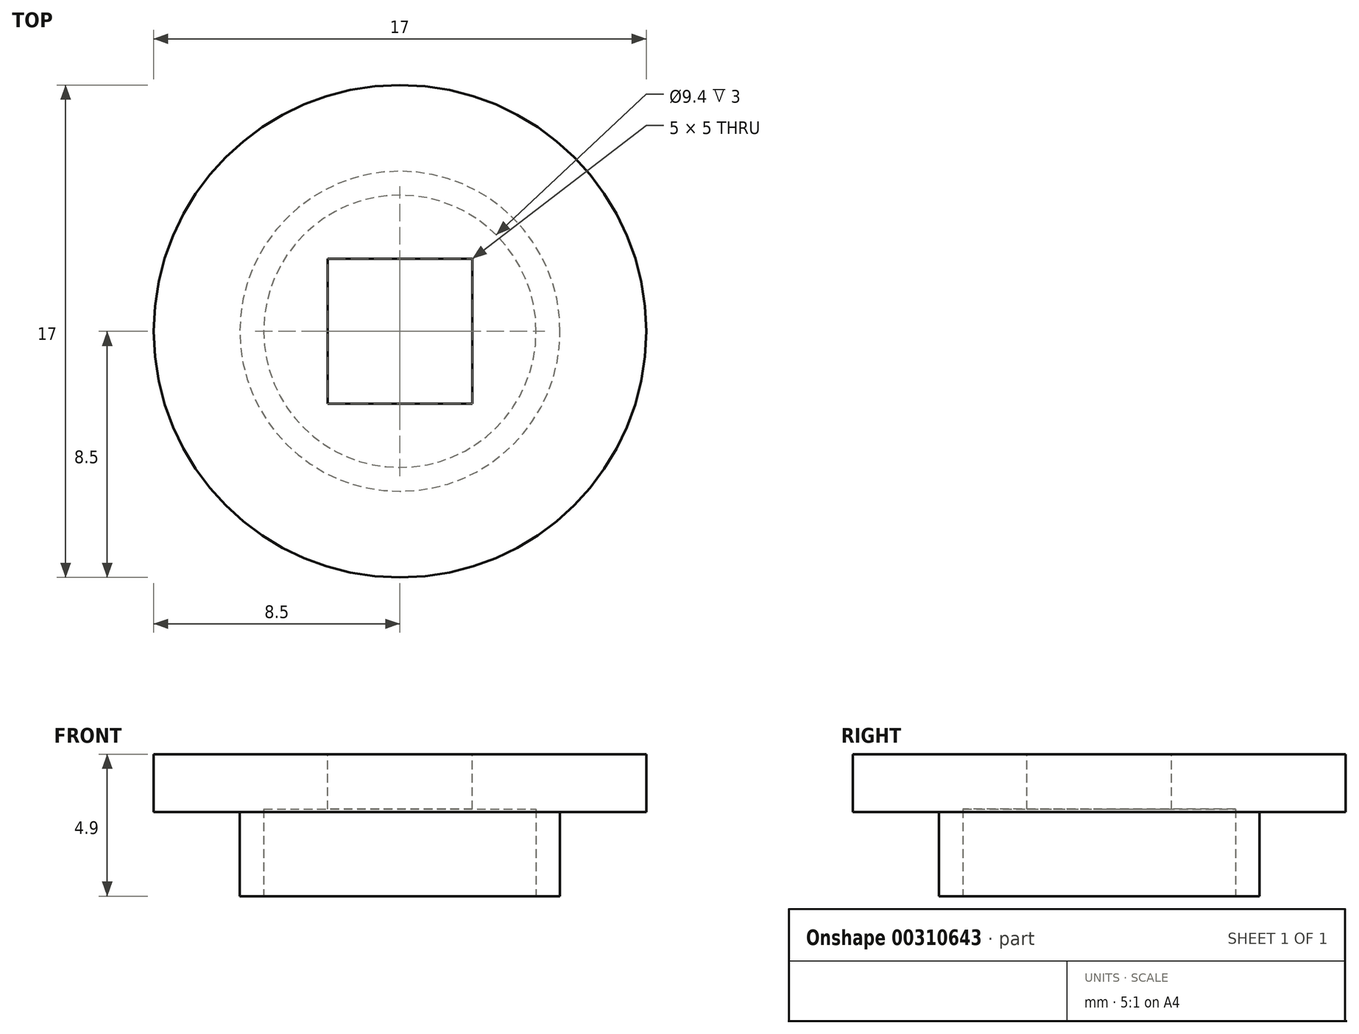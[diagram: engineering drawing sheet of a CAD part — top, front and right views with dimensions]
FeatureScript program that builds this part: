
annotation { "Feature Type Name" : "Feature", "Feature Type Description" : "" }
export const myFeature = defineFeature(function(context is Context, id is Id, definition is map)
    precondition{}
    {
        {
            var Q0;
            Q0=qCreatedBy(makeId("Top.planeOp"),FACE);
            var sketch = newSketch(context, id + "F0", { "sketchPlane" : qUnion([Q0])});
            skCircle(sketch, "E0", {"center": v(0, 0) * mm, "radius": 8.5 * mm});
            skSolve(sketch);
        }
        {
            var Q0;
            Q0 = qSketchRegion(id + "F0", true);
            extrude(context, id + "F1", {"entities" : qUnion([Q0]), "depth" : 2 * mm});
        }
        {
            var Q0;
            Q0=makeQuery(id+"F1.opExtrude","CAP_FACE",FACE,{"disambiguationData":[OSD([sQuery(id+"F0.wireOp",EDGE,"E0")])],"isStart":true});
            var sketch = newSketch(context, id + "F2", { "sketchPlane" : qUnion([Q0])});
            skCircle(sketch, "E1", {"center": v(0, 0) * mm, "radius": 5.53 * mm});
            skSolve(sketch);
        }
        {
            var Q0;
            Q0 = qSketchRegion(id + "F2", true);
            extrude(context, id + "F3", {"entities" : qUnion([Q0]), "operationType" : NewBodyOperationType.ADD, "depth" : 2.9 * mm});
        }
        {
            var Q0;
            Q0=makeQuery(id+"F3.opExtrude","CAP_FACE",FACE,{"disambiguationData":[OSD([sQuery(id+"F2.wireOp",EDGE,"E1")])],"isStart":false});
            var sketch = newSketch(context, id + "F4", { "sketchPlane" : qUnion([Q0])});
            skCircle(sketch, "E2", {"center": v(0, 0) * mm, "radius": 4.7 * mm});
            skSolve(sketch);
        }
        {
            var Q0;
            Q0 = qSketchRegion(id + "F4", true);
            extrude(context, id + "F5", {"entities" : qUnion([Q0]), "operationType" : NewBodyOperationType.REMOVE, "oppositeDirection" : true, "depth" : 3 * mm});
        }
        {
            var Q0;
            Q0=makeQuery(id+"F1.opExtrude","CAP_FACE",FACE,{"disambiguationData":[OSD([sQuery(id+"F0.wireOp",EDGE,"E0")])],"isStart":false});
            var sketch = newSketch(context, id + "F6", { "sketchPlane" : qUnion([Q0])});
            skLineSegment(sketch, "E3.bottom", {"start": v(-2.5, 2.5) * mm, "end": v(2.5, 2.5) * mm});
            skLineSegment(sketch, "E3.top", {"start": v(-2.5, -2.5) * mm, "end": v(2.5, -2.5) * mm});
            skLineSegment(sketch, "E3.left", {"start": v(-2.5, 2.5) * mm, "end": v(-2.5, -2.5) * mm});
            skLineSegment(sketch, "E3.right", {"start": v(2.5, 2.5) * mm, "end": v(2.5, -2.5) * mm});
            skPoint(sketch, "E3.middle", {"position": v(0, 0) * mm});
            skSolve(sketch);
        }
        {
            var Q0;
            Q0 = qSketchRegion(id + "F6", true);
            extrude(context, id + "F7", {"entities" : qUnion([Q0]), "operationType" : NewBodyOperationType.REMOVE, "oppositeDirection" : true, "depth" : 25 * mm});
        }
    });
